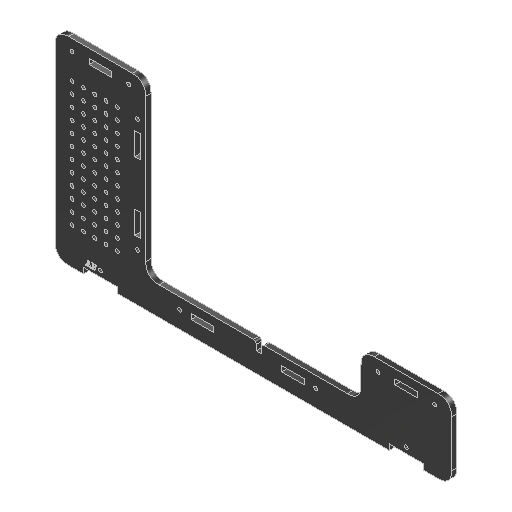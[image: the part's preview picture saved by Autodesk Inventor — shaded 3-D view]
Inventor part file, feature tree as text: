
AUTODESK INVENTOR PART (.ipt)
format: ipt  version: 2025 (Build 290162000, 162)  size: 438,272 bytes
history: native  units: mm
features: sketch x7, extrude x4, hole x3, fillet x2, pattern_linear x1, emboss x1, projected_geometry x1
ambient origin geometry x8: Origin, YZ Plane, XZ Plane, XY Plane, X Axis, Y Axis, Z Axis, Center Point
bodies: Solid1 (feature_tree)
feature tree (19):
  extrude  "Extrusion1"  Depth=222.25mm
  extrude  "Extrusion2"  Depth=241.3mm
  sketch  "Sketch3"  dims[d7=6.0mm d9=6.0mm d10=0.0mm]
  hole  "Hole3"  [1 undecoded]
  hole  "Hole2"  [1 undecoded]
  pattern_linear  "Rectangular Pattern1"  Spacing1=19.05mm  [1 undecoded]
  extrude  "Extrusion3"  Depth=120.0mm
  hole  "Hole1"  [1 undecoded]
  extrude  "Extrusion4"  Depth=76.2mm
  fillet  "Fillet1"  Radius=127.0mm
  fillet  "Fillet2"  Radius=152.4mm
  emboss  "Emboss1"
  sketch  "Sketch1"  dims[d0=6.0mm d1=0.0mm d2=222.25mm]
  sketch  "Sketch2"  dims[d3=101.6mm d4=241.3mm]
  sketch  "Sketch4"  dims[d11=6.35mm d12=38.1mm]
  sketch  "Sketch5"  dims[d14=6.0mm d15=0.0mm]
  projected_geometry  "Projected Loop1"
  sketch  "Sketch6"  dims[d16=4.25mm d17=6.0mm d18=4.0mm d19=2.0mm d20=90.0deg d21=8.0mm d22=20.594885mm]
  sketch  "Sketch7"  dims[d23=15.0mm d25=19.05mm d26=4.25mm d27=6.0mm d28=4.0mm d29=2.0mm d30=90.0deg d31=8.0mm d32=20.594885mm d33=120.0mm d35=12.7mm d36=50.0mm d38=12.7mm d39=4.25mm d40=6.0mm d41=4.0mm d42=2.0mm d43=90.0deg d44=8.0mm d45=20.594885mm d47=63.5mm d50=76.2mm d52=127.0mm d53=152.4mm d76=139.7mm d79=25.4mm d80=31.75mm d91=190.5mm d92=180.8mm d93=50.8mm d94=165.1mm d95=342.9mm d97=209.55mm d98=12.7mm d99=89.450001mm d100=76.2mm d103=6.0mm d104=9.525mm d105=228.6mm d106=25.4mm d107=0.0mm d108=3.175mm d109=2.54mm d110=0.0mm d111=31.75mm d112=82.55mm]
note: 4 required parameter values undecoded (feature->parameter linkage not recoverable at this tier; creation-order binding heuristic only, values carry confidence <= 0.55)
